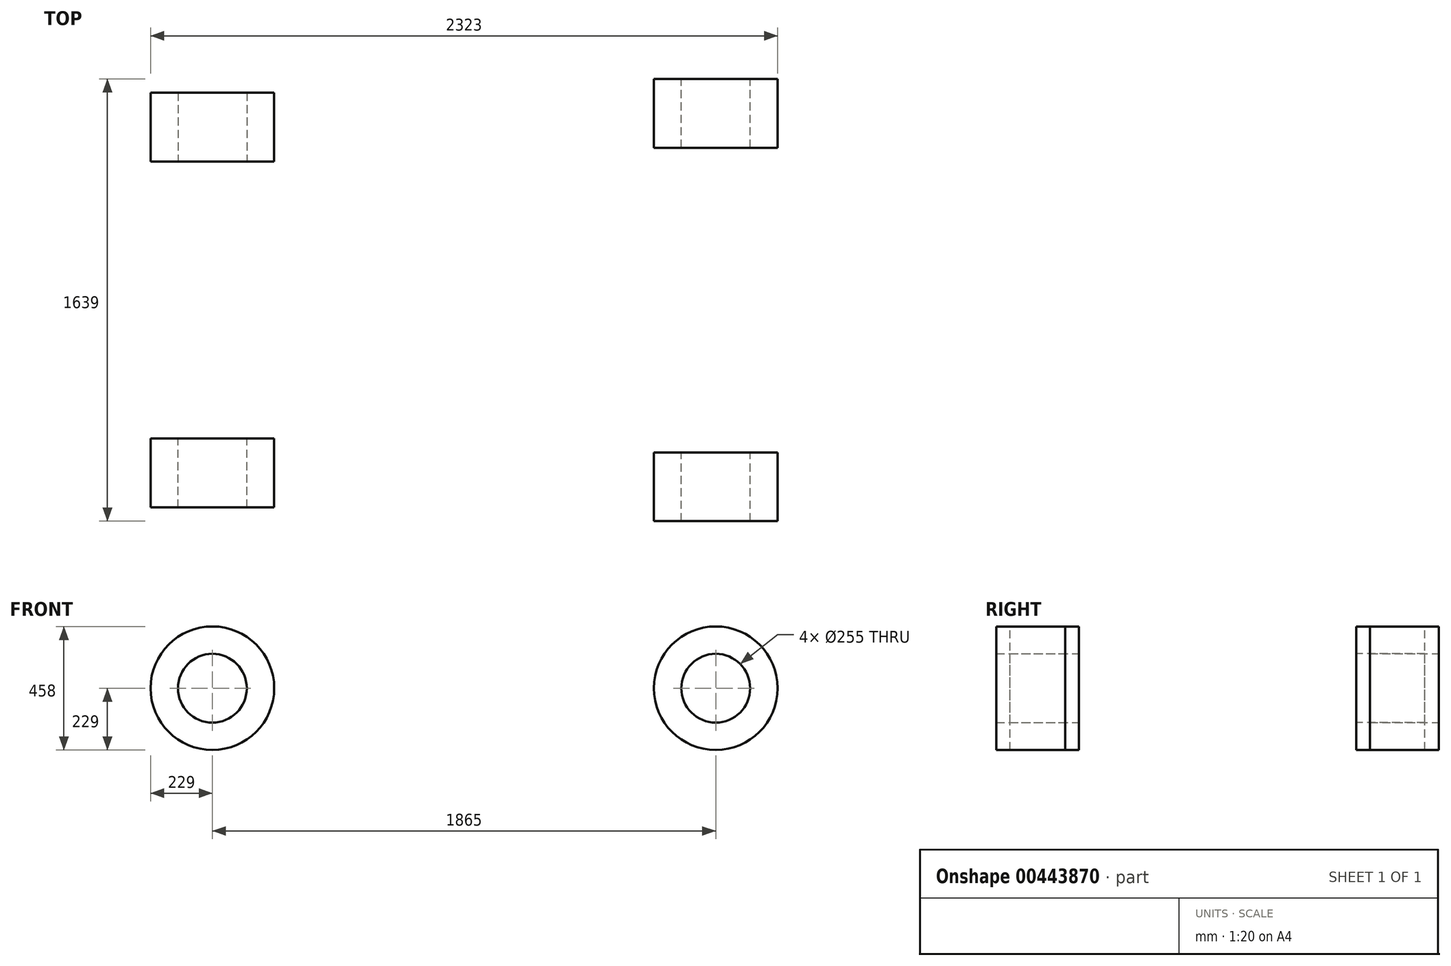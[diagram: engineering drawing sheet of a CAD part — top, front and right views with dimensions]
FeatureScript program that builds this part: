
annotation { "Feature Type Name" : "Feature", "Feature Type Description" : "" }
export const myFeature = defineFeature(function(context is Context, id is Id, definition is map)
    precondition{}
    {
        {
            var Q0;
            Q0=qCreatedBy(makeId("Top.planeOp"),FACE);
            var sketch = newSketch(context, id + "F0", { "sketchPlane" : qUnion([Q0])});
            skLineSegment(sketch, "E0", {"start": v(0, 750) * mm, "end": v(0, -750) * mm, "construction": true});
            skLineSegment(sketch, "E1", {"start": v(-1500, 0) * mm, "end": v(1500, 0) * mm, "construction": true});
            skSolve(sketch);
        }
        {
            var Q0;
            Q0=qCreatedBy(makeId("Front.planeOp"),FACE);
            cPlane(context, id + "F1", {"entities" : qUnion([Q0]), "cplaneType" : CPlaneType.OFFSET, "offset" : 692 * mm, "width" : 150 * mm, "height" : 150 * mm});
        }
        {
            var Q0;
            Q0=qCreatedBy(id+"F1.planeOp",FACE);
            var sketch = newSketch(context, id + "F2", { "sketchPlane" : qUnion([Q0])});
            skCircle(sketch, "E2", {"center": v(932.5, 0) * mm, "radius": 127.5 * mm});
            skCircle(sketch, "E3", {"center": v(932.5, 0) * mm, "radius": 229 * mm});
            skSolve(sketch);
        }
        {
            var Q0;
            Q0=makeQuery(id+"F2.imprint","IMPRINT",FACE,{"disambiguationData":[TD([[makeQuery(id+"F2.imprint","IMPRINT",EDGE,{"derivedFrom":sQuery(id+"F2.wireOp",EDGE,"E2")}),-1.0]])]});
            extrude(context, id + "F3", {"entities" : qUnion([Q0]), "endBound" : BoundingType.SYMMETRIC, "oppositeDirection" : true, "depth" : 255 * mm});
        }
        {
            var Q0;
            Q0=makeQuery(id+"F2.imprint","IMPRINT",FACE,{"disambiguationData":[TD([[makeQuery(id+"F2.imprint","IMPRINT",EDGE,{"derivedFrom":sQuery(id+"F2.wireOp",EDGE,"E2")}),1.0]])]});
            extrude(context, id + "F4", {"entities" : qUnion([Q0]), "endBound" : BoundingType.SYMMETRIC, "depth" : 255 * mm});
        }
        {
            var Q0;
            Q0=makeQuery(id+"F3.opExtrude","SWEPT_BODY",BODY,{"disambiguationData":[OSD([sQuery(id+"F2.wireOp",EDGE,"E2"),sQuery(id+"F2.wireOp",EDGE,"E3")])]});
            var Q1;
            Q1=makeQuery(id+"F4.opExtrude","SWEPT_BODY",BODY,{"disambiguationData":[OSD([sQuery(id+"F2.wireOp",EDGE,"E2")])]});
            var Q2;
            Q2=qCreatedBy(makeId("Front.planeOp"),FACE);
            mirror(context, id + "F5", {"entities" : qUnion([Q0, Q1]), "mirrorPlane" : qUnion([Q2])});
        }
        {
            var Q0;
            Q0=qCreatedBy(makeId("Front.planeOp"),FACE);
            cPlane(context, id + "F6", {"entities" : qUnion([Q0]), "cplaneType" : CPlaneType.OFFSET, "offset" : 641 * mm, "width" : 150 * mm, "height" : 150 * mm});
        }
        {
            var Q0;
            Q0=qCreatedBy(id+"F6.planeOp",FACE);
            var sketch = newSketch(context, id + "F7", { "sketchPlane" : qUnion([Q0])});
            skCircle(sketch, "E4", {"center": v(-932.5, 0) * mm, "radius": 127.5 * mm});
            skCircle(sketch, "E5", {"center": v(-932.5, 0) * mm, "radius": 229 * mm});
            skSolve(sketch);
        }
        {
            var Q0;
            Q0=makeQuery(id+"F7.imprint","IMPRINT",FACE,{"disambiguationData":[TD([[makeQuery(id+"F7.imprint","IMPRINT",EDGE,{"derivedFrom":sQuery(id+"F7.wireOp",EDGE,"E4")}),-1.0]])]});
            extrude(context, id + "F8", {"entities" : qUnion([Q0]), "endBound" : BoundingType.SYMMETRIC, "depth" : 255 * mm});
        }
        {
            var Q0;
            Q0=makeQuery(id+"F7.imprint","IMPRINT",FACE,{"disambiguationData":[TD([[makeQuery(id+"F7.imprint","IMPRINT",EDGE,{"derivedFrom":sQuery(id+"F7.wireOp",EDGE,"E4")}),1.0]])]});
            extrude(context, id + "F9", {"entities" : qUnion([Q0]), "endBound" : BoundingType.SYMMETRIC, "depth" : 255 * mm});
        }
        {
            var Q0;
            Q0=makeQuery(id+"F8.opExtrude","SWEPT_BODY",BODY,{"disambiguationData":[OSD([sQuery(id+"F7.wireOp",EDGE,"E4"),sQuery(id+"F7.wireOp",EDGE,"E5")])]});
            var Q1;
            Q1=makeQuery(id+"F9.opExtrude","SWEPT_BODY",BODY,{"disambiguationData":[OSD([sQuery(id+"F7.wireOp",EDGE,"E4")])]});
            var Q2;
            Q2=qCreatedBy(makeId("Front.planeOp"),FACE);
            mirror(context, id + "F10", {"entities" : qUnion([Q0, Q1]), "mirrorPlane" : qUnion([Q2])});
        }
    });
